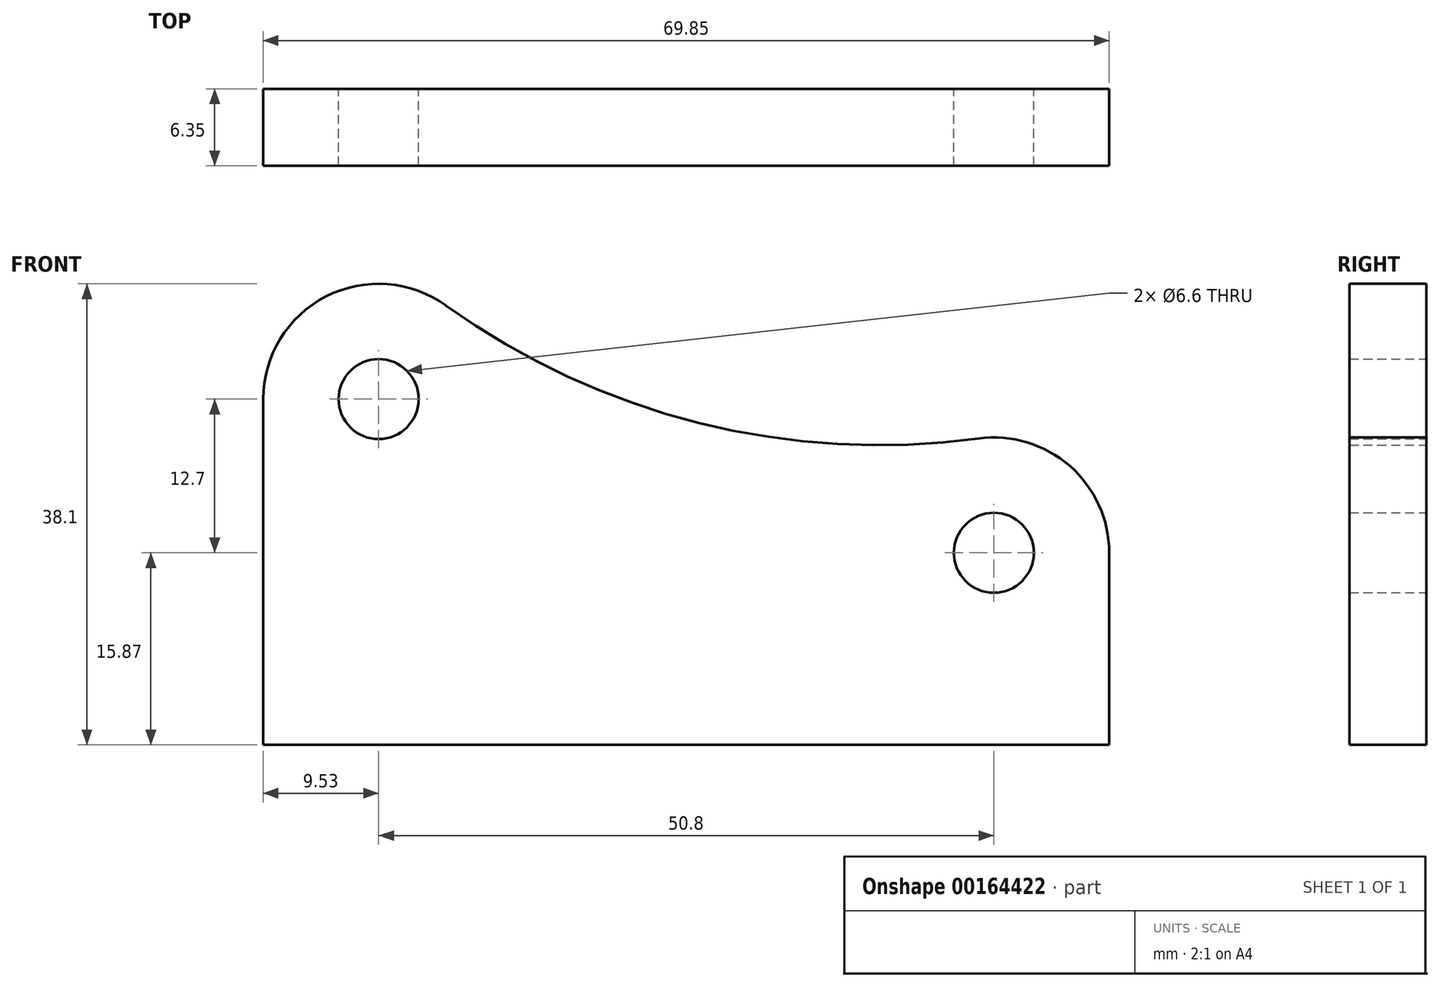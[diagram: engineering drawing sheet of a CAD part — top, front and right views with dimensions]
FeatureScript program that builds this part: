
annotation { "Feature Type Name" : "Feature", "Feature Type Description" : "" }
export const myFeature = defineFeature(function(context is Context, id is Id, definition is map)
    precondition{}
    {
        {
            var Q0;
            Q0=qCreatedBy(makeId("Front.planeOp"),FACE);
            var sketch = newSketch(context, id + "F0", { "sketchPlane" : qUnion([Q0])});
            skLineSegment(sketch, "E0", {"start": v(0, 0) * mm, "end": v(50.8, -12.7) * mm, "construction": true});
            skLineSegment(sketch, "E1", {"start": v(50.8, -12.7) * mm, "end": v(0, -12.7) * mm, "construction": true});
            skLineSegment(sketch, "E2", {"start": v(0, -12.7) * mm, "end": v(0, 0) * mm, "construction": true});
            skCircle(sketch, "E3", {"center": v(0, 0) * mm, "radius": 3.3 * mm});
            skCircle(sketch, "E4", {"center": v(50.8, -12.7) * mm, "radius": 3.3 * mm});
            skLineSegment(sketch, "E5", {"start": v(-9.53, 0) * mm, "end": v(-9.53, -28.57) * mm});
            skLineSegment(sketch, "E6", {"start": v(-9.52, -28.57) * mm, "end": v(60.33, -28.57) * mm});
            skLineSegment(sketch, "E7", {"start": v(60.33, -28.58) * mm, "end": v(60.33, -12.7) * mm});
            skArc(sketch, "E8", {"start": v(60.33, -12.7) * mm, "mid": v(57.07, -5.53) * mm, "end": v(49.53, -3.26) * mm});
            skArc(sketch, "E9", {"start": v(5.57, 7.73) * mm, "mid": v(-4.34, 8.48) * mm, "end": v(-9.53, 0) * mm});
            skArc(sketch, "E10", {"start": v(5.57, 7.73) * mm, "mid": v(26.5, -1.98) * mm, "end": v(49.53, -3.26) * mm});
            skPoint(sketch, "E11.orphan", {"position": v(9.53, 0) * mm});
            skLineSegment(sketch, "E12", {"start": v(50.8, -12.7) * mm, "end": v(50.8, -3.8) * mm, "construction": true});
            skLineSegment(sketch, "E13", {"start": v(50.8, -3.8) * mm, "end": v(15.24, -3.8) * mm, "construction": true});
            skSolve(sketch);
        }
        {
            var Q0;
            Q0 = qSketchRegion(id + "F0", true);
            extrude(context, id + "F1", {"entities" : qUnion([Q0]), "depth" : 6.35 * mm});
        }
    });
